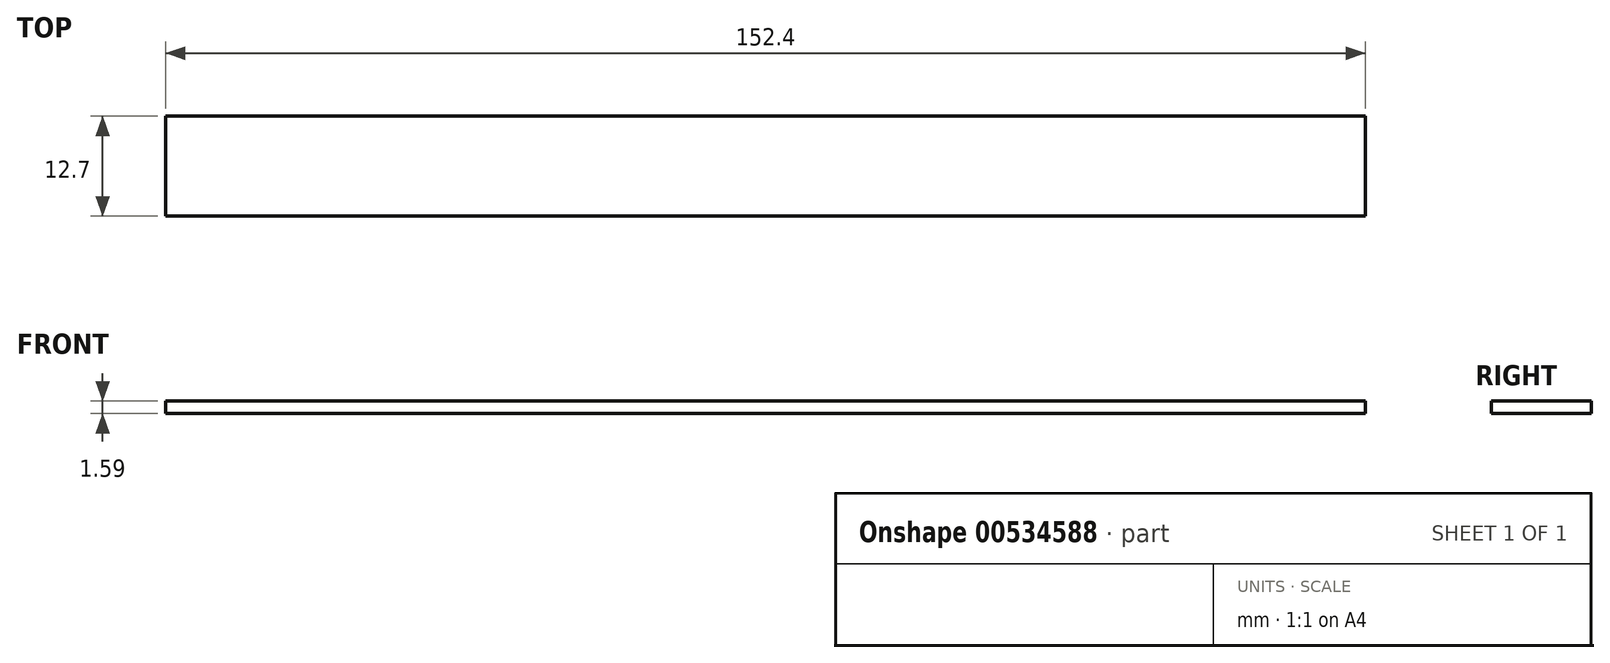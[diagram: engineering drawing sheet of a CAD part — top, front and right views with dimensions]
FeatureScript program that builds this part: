
annotation { "Feature Type Name" : "Feature", "Feature Type Description" : "" }
export const myFeature = defineFeature(function(context is Context, id is Id, definition is map)
    precondition{}
    {
        {
            var Q0;
            Q0=qCreatedBy(makeId("Top.planeOp"),FACE);
            var sketch = newSketch(context, id + "F0", { "sketchPlane" : qUnion([Q0])});
            skLineSegment(sketch, "E0.bottom", {"start": v(0, 0) * mm, "end": v(-152.4, 0) * mm});
            skLineSegment(sketch, "E0.top", {"start": v(0, 12.7) * mm, "end": v(-152.4, 12.7) * mm});
            skLineSegment(sketch, "E0.left", {"start": v(0, 0) * mm, "end": v(0, 12.7) * mm});
            skLineSegment(sketch, "E0.right", {"start": v(-152.4, 0) * mm, "end": v(-152.4, 12.7) * mm});
            skSolve(sketch);
        }
        {
            var Q0;
            Q0=makeQuery(id+"F0.imprint","IMPRINT",FACE,{"disambiguationData":[TD([[makeQuery(id+"F0.imprint","IMPRINT",EDGE,{"derivedFrom":sQuery(id+"F0.wireOp",EDGE,"E0.bottom")}),-1.0]])]});
            extrude(context, id + "F1", {"entities" : qUnion([Q0]), "depth" : 1.59 * mm, "offsetDistance" : 25.4 * mm});
        }
    });
